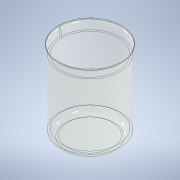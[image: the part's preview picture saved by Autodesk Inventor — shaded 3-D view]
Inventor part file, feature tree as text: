
AUTODESK INVENTOR PART (.ipt)
format: ipt  version: 2020 (Build 240168000, 168)  size: 220,672 bytes
history: native  units: mm
features: revolve x1, sketch x1
ambient origin geometry x8: Origin, YZ Plane, XZ Plane, XY Plane, X Axis, Y Axis, Z Axis, Center Point
bodies: Solid1 (feature_tree)
feature tree (2):
  revolve  "Revolution1"  [1 undecoded]
  sketch  "Sketch1"  dims[d0=45.0mm d1=2.0mm d2=42.0mm d3=90.0deg d4=118.0mm d5=90.0deg d6=2.0mm d7=2.0mm d8=90.0deg d9=12.0mm d10=0.5mm d11=0.5mm d12=9.0mm d13=9.0mm d14=90.0deg d15=0.872665mm d16=0.872665mm]
note: 1 required parameter value undecoded (feature->parameter linkage not recoverable at this tier; creation-order binding heuristic only, values carry confidence <= 0.55)
